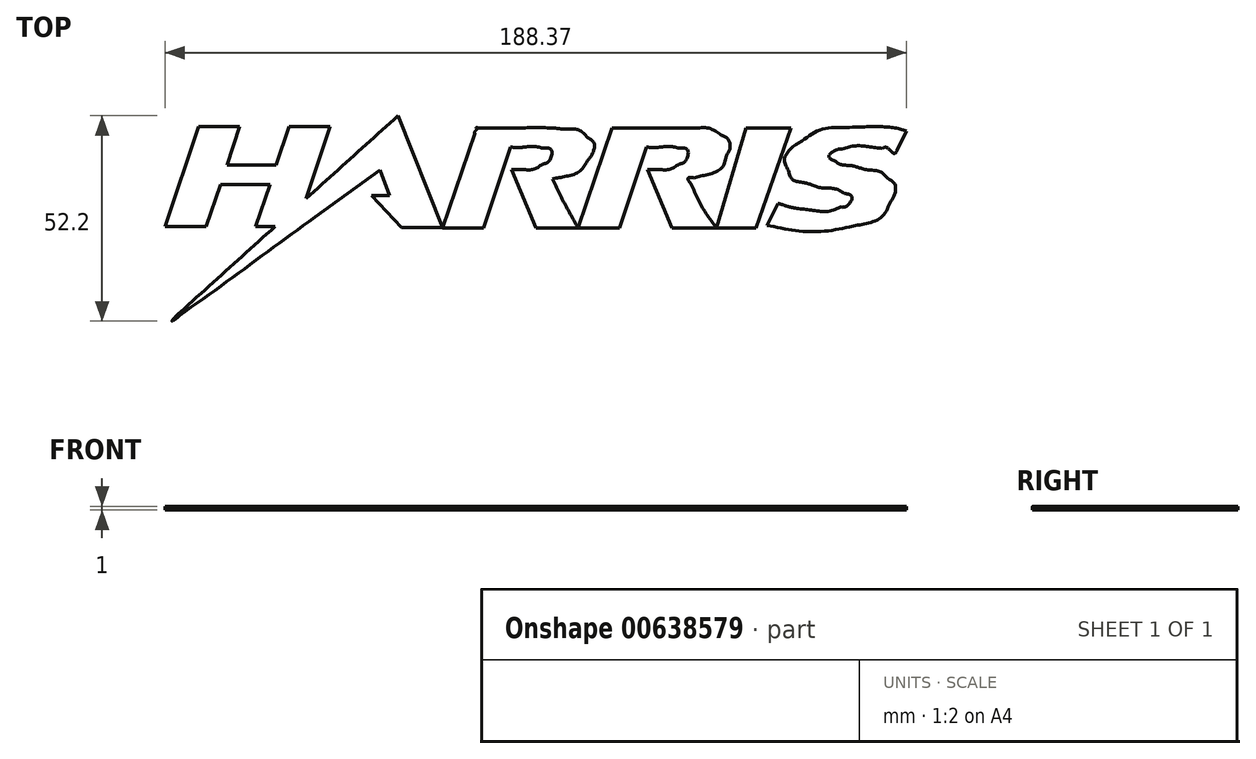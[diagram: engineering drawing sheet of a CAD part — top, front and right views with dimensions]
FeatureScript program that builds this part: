
annotation { "Feature Type Name" : "Feature", "Feature Type Description" : "" }
export const myFeature = defineFeature(function(context is Context, id is Id, definition is map)
    precondition{}
    {
        {
            var Q0;
            Q0=qCreatedBy(makeId("Top.planeOp"),FACE);
            var sketch = newSketch(context, id + "F0", { "sketchPlane" : qUnion([Q0])});
            skFitSpline(sketch, "E0", {"points": [v(65, 22.87) * mm, v(59.37, 22.73) * mm, v(53.44, 22.23) * mm, v(48.5, 19.25) * mm]});
            skFitSpline(sketch, "E1", {"points": [v(48.5, 19.25) * mm, v(46.1, 17.74) * mm, v(44, 14.7) * mm, v(45.01, 11.78) * mm]});
            skFitSpline(sketch, "E2", {"points": [v(45.01, 11.78) * mm, v(46.07, 9.46) * mm, v(48.77, 8.71) * mm, v(51.04, 8.09) * mm]});
            skFitSpline(sketch, "E3", {"points": [v(51.04, 8.09) * mm, v(53.74, 7.3) * mm, v(56.65, 7.17) * mm, v(59.22, 5.95) * mm]});
            skFitSpline(sketch, "E4", {"points": [v(59.22, 5.95) * mm, v(61.14, 5.03) * mm, v(59.79, 2.74) * mm, v(58.18, 2.44) * mm]});
            skFitSpline(sketch, "E5", {"points": [v(58.18, 2.44) * mm, v(54.76, 1.33) * mm, v(51.07, 1.66) * mm, v(47.55, 2.08) * mm]});
            skFitSpline(sketch, "E6", {"points": [v(47.55, 2.08) * mm, v(45.8, 2.37) * mm, v(44.07, 2.88) * mm, v(42.37, 3.4) * mm]});
            skFitSpline(sketch, "E7", {"points": [v(42.37, 3.4) * mm, v(41.43, 1.55) * mm, v(40.5, -0.3) * mm, v(39.57, -2.15) * mm]});
            skFitSpline(sketch, "E8", {"points": [v(39.57, -2.15) * mm, v(46.47, -3.44) * mm, v(53.6, -3.71) * mm, v(60.53, -2.54) * mm]});
            skFitSpline(sketch, "E9", {"points": [v(60.53, -2.54) * mm, v(64.47, -1.76) * mm, v(68.66, -0.09) * mm, v(70.77, 3.54) * mm]});
            skFitSpline(sketch, "E10", {"points": [v(70.77, 3.54) * mm, v(71.9, 5.4) * mm, v(72.08, 8.13) * mm, v(70.32, 9.67) * mm]});
            skFitSpline(sketch, "E11", {"points": [v(70.32, 9.67) * mm, v(68.23, 11.51) * mm, v(65.34, 11.9) * mm, v(62.73, 12.54) * mm]});
            skFitSpline(sketch, "E12", {"points": [v(62.73, 12.54) * mm, v(60.76, 13.03) * mm, v(58.65, 13.2) * mm, v(56.82, 14.13) * mm]});
            skFitSpline(sketch, "E13", {"points": [v(56.82, 14.13) * mm, v(55.27, 15.4) * mm, v(57.28, 17.05) * mm, v(58.65, 17.24) * mm]});
            skFitSpline(sketch, "E14", {"points": [v(58.65, 17.24) * mm, v(62, 18.03) * mm, v(65.5, 17.8) * mm, v(68.88, 17.36) * mm]});
            skFitSpline(sketch, "E15", {"points": [v(68.88, 17.36) * mm, v(70.04, 17.6) * mm, v(71.86, 16.04) * mm, v(72.58, 16.89) * mm]});
            skFitSpline(sketch, "E16", {"points": [v(72.58, 16.89) * mm, v(73.39, 18.54) * mm, v(74.2, 20.18) * mm, v(75, 21.83) * mm]});
            skFitSpline(sketch, "E17", {"points": [v(75, 21.83) * mm, v(71.75, 22.62) * mm, v(68.34, 22.89) * mm, v(65, 22.87) * mm]});
            skLineSegment(sketch, "E18", {"start": v(-104.86, 22.9) * mm, "end": v(-113.37, -2.5) * mm});
            skLineSegment(sketch, "E19", {"start": v(-113.37, -2.5) * mm, "end": v(-102.93, -2.5) * mm});
            skLineSegment(sketch, "E20", {"start": v(-102.93, -2.5) * mm, "end": v(-99.31, 8.26) * mm});
            skLineSegment(sketch, "E21", {"start": v(-99.31, 8.26) * mm, "end": v(-86.73, 8.26) * mm});
            skLineSegment(sketch, "E22", {"start": v(-86.73, 8.26) * mm, "end": v(-90.35, -2.5) * mm});
            skLineSegment(sketch, "E23", {"start": v(-90.35, -2.5) * mm, "end": v(-85.18, -2.5) * mm});
            skLineSegment(sketch, "E24", {"start": v(-85.18, -2.5) * mm, "end": v(-77.6, 4.33) * mm});
            skLineSegment(sketch, "E25", {"start": v(-77.6, 4.33) * mm, "end": v(-71.4, 22.9) * mm});
            skLineSegment(sketch, "E26", {"start": v(-71.4, 22.9) * mm, "end": v(-81.84, 22.9) * mm});
            skLineSegment(sketch, "E27", {"start": v(-81.84, 22.9) * mm, "end": v(-85.11, 13.15) * mm});
            skLineSegment(sketch, "E28", {"start": v(-85.11, 13.15) * mm, "end": v(-97.66, 13.15) * mm});
            skLineSegment(sketch, "E29", {"start": v(-97.66, 13.15) * mm, "end": v(-94.38, 22.9) * mm});
            skLineSegment(sketch, "E30", {"start": v(-94.38, 22.9) * mm, "end": v(-104.86, 22.9) * mm});
            skLineSegment(sketch, "E31", {"start": v(-104.86, 22.9) * mm, "end": v(-104.86, 22.9) * mm});
            skFitSpline(sketch, "E32", {"points": [v(-11.94, 3.53) * mm, v(-13.01, 5.53) * mm, v(-13.98, 7.58) * mm, v(-14.94, 9.63) * mm]});
            skFitSpline(sketch, "E33", {"points": [v(-14.94, 9.63) * mm, v(-11.66, 10.25) * mm, v(-8.13, 11.47) * mm, v(-6.07, 14.26) * mm]});
            skFitSpline(sketch, "E34", {"points": [v(-6.07, 14.26) * mm, v(-4.83, 15.93) * mm, v(-4.36, 18.58) * mm, v(-6.03, 20.14) * mm]});
            skFitSpline(sketch, "E35", {"points": [v(-6.03, 20.14) * mm, v(-8.27, 22.06) * mm, v(-11.39, 22.3) * mm, v(-14.2, 22.52) * mm]});
            skFitSpline(sketch, "E36", {"points": [v(-14.2, 22.52) * mm, v(-19.17, 22.67) * mm, v(-24.14, 22.56) * mm, v(-29.1, 22.6) * mm]});
            skFitSpline(sketch, "E37", {"points": [v(-29.1, 22.6) * mm, v(-30.88, 22.6) * mm, v(-32.67, 22.6) * mm, v(-34.45, 22.6) * mm]});
            skFitSpline(sketch, "E38", {"points": [v(-34.45, 22.6) * mm, v(-33.92, 22.6) * mm, v(-34.66, 21.63) * mm, v(-34.67, 21.22) * mm]});
            skFitSpline(sketch, "E39", {"points": [v(-34.67, 21.22) * mm, v(-37.38, 13.22) * mm, v(-40.1, 5.21) * mm, v(-42.81, -2.8) * mm]});
            skFitSpline(sketch, "E40", {"points": [v(-42.81, -2.8) * mm, v(-39.38, -2.8) * mm, v(-35.95, -2.8) * mm, v(-32.52, -2.8) * mm]});
            skFitSpline(sketch, "E41", {"points": [v(-32.52, -2.8) * mm, v(-30.22, 4.03) * mm, v(-27.92, 10.86) * mm, v(-25.63, 17.7) * mm]});
            skFitSpline(sketch, "E42", {"points": [v(-25.63, 17.7) * mm, v(-22.86, 17.63) * mm, v(-20.06, 17.89) * mm, v(-17.32, 17.42) * mm]});
            skFitSpline(sketch, "E43", {"points": [v(-17.32, 17.42) * mm, v(-15.18, 17) * mm, v(-15.88, 14.1) * mm, v(-17.45, 13.4) * mm]});
            skFitSpline(sketch, "E44", {"points": [v(-17.45, 13.4) * mm, v(-19.84, 12.06) * mm, v(-22.7, 12.01) * mm, v(-25.38, 12.01) * mm]});
            skFitSpline(sketch, "E45", {"points": [v(-25.38, 12.01) * mm, v(-23.32, 7.07) * mm, v(-21.25, 2.13) * mm, v(-19.18, -2.8) * mm]});
            skFitSpline(sketch, "E46", {"points": [v(-19.18, -2.8) * mm, v(-15.6, -2.81) * mm, v(-12.02, -2.82) * mm, v(-8.44, -2.83) * mm]});
            skFitSpline(sketch, "E47", {"points": [v(-8.44, -2.83) * mm, v(-9.62, -0.71) * mm, v(-10.8, 1.4) * mm, v(-11.94, 3.53) * mm]});
            skLineSegment(sketch, "E48", {"start": v(-11.94, 3.53) * mm, "end": v(-11.94, 3.53) * mm});
            skFitSpline(sketch, "E49", {"points": [v(2.09, -2.8) * mm, v(4.39, 4.03) * mm, v(6.68, 10.86) * mm, v(8.98, 17.7) * mm]});
            skFitSpline(sketch, "E50", {"points": [v(8.98, 17.7) * mm, v(11.75, 17.63) * mm, v(14.55, 17.89) * mm, v(17.29, 17.42) * mm]});
            skFitSpline(sketch, "E51", {"points": [v(17.29, 17.42) * mm, v(19.42, 17) * mm, v(18.78, 14.1) * mm, v(17.2, 13.4) * mm]});
            skFitSpline(sketch, "E52", {"points": [v(17.2, 13.4) * mm, v(14.79, 12.06) * mm, v(11.92, 12.01) * mm, v(9.22, 12.01) * mm]});
            skFitSpline(sketch, "E53", {"points": [v(9.22, 12.01) * mm, v(11.3, 7.07) * mm, v(13.36, 2.13) * mm, v(15.43, -2.8) * mm]});
            skFitSpline(sketch, "E54", {"points": [v(15.43, -2.8) * mm, v(19.2, -2.8) * mm, v(22.96, -2.8) * mm, v(26.73, -2.8) * mm]});
            skFitSpline(sketch, "E55", {"points": [v(26.73, -2.8) * mm, v(24.2, 0.67) * mm, v(22.04, 4.4) * mm, v(20.28, 8.32) * mm]});
            skFitSpline(sketch, "E56", {"points": [v(20.28, 8.32) * mm, v(19.56, 9.33) * mm, v(19.6, 9.92) * mm, v(20.96, 9.89) * mm]});
            skFitSpline(sketch, "E57", {"points": [v(20.96, 9.89) * mm, v(24.23, 10.7) * mm, v(27.9, 12.24) * mm, v(29.28, 15.58) * mm]});
            skFitSpline(sketch, "E58", {"points": [v(29.28, 15.58) * mm, v(30.12, 17.32) * mm, v(29.7, 19.66) * mm, v(27.95, 20.68) * mm]});
            skFitSpline(sketch, "E59", {"points": [v(27.95, 20.68) * mm, v(24.92, 22.46) * mm, v(21.28, 22.52) * mm, v(17.87, 22.6) * mm]});
            skFitSpline(sketch, "E60", {"points": [v(17.87, 22.6) * mm, v(11.97, 22.6) * mm, v(6.06, 22.6) * mm, v(0.16, 22.6) * mm]});
            skFitSpline(sketch, "E61", {"points": [v(0.16, 22.6) * mm, v(-2.7, 14.12) * mm, v(-5.57, 5.65) * mm, v(-8.44, -2.83) * mm]});
            skFitSpline(sketch, "E62", {"points": [v(-8.44, -2.83) * mm, v(-4.93, -2.82) * mm, v(-1.42, -2.81) * mm, v(2.09, -2.8) * mm]});
            skLineSegment(sketch, "E63", {"start": v(2.09, -2.8) * mm, "end": v(2.09, -2.8) * mm});
            skLineSegment(sketch, "E64", {"start": v(36.8, -2.8) * mm, "end": v(45.66, 22.6) * mm});
            skLineSegment(sketch, "E65", {"start": v(45.66, 22.6) * mm, "end": v(34.26, 22.6) * mm});
            skLineSegment(sketch, "E66", {"start": v(34.26, 22.6) * mm, "end": v(26.73, -2.8) * mm});
            skLineSegment(sketch, "E67", {"start": v(26.73, -2.8) * mm, "end": v(36.8, -2.8) * mm});
            skFitSpline(sketch, "E68", {"points": [v(-54.16, 25.67) * mm, v(-72.6, 9.04) * mm, v(-91.05, -7.56) * mm, v(-109.48, -24.2) * mm]});
            skFitSpline(sketch, "E69", {"points": [v(-109.48, -24.2) * mm, v(-110.47, -25.16) * mm, v(-111.61, -26.52) * mm, v(-109.72, -25.12) * mm]});
            skFitSpline(sketch, "E70", {"points": [v(-109.72, -25.12) * mm, v(-98.17, -16.86) * mm, v(-86.75, -8.43) * mm, v(-75.25, -0.1) * mm]});
            skFitSpline(sketch, "E71", {"points": [v(-75.25, -0.1) * mm, v(-69.75, 3.9) * mm, v(-64.24, 7.9) * mm, v(-58.74, 11.9) * mm]});
            skFitSpline(sketch, "E72", {"points": [v(-58.74, 11.9) * mm, v(-57.95, 9.74) * mm, v(-57.16, 7.58) * mm, v(-56.37, 5.4) * mm]});
            skFitSpline(sketch, "E73", {"points": [v(-56.37, 5.4) * mm, v(-57.89, 5.4) * mm, v(-59.4, 5.4) * mm, v(-60.92, 5.4) * mm]});
            skFitSpline(sketch, "E74", {"points": [v(-60.92, 5.4) * mm, v(-58.37, 2.68) * mm, v(-55.82, -0.04) * mm, v(-53.27, -2.77) * mm]});
            skFitSpline(sketch, "E75", {"points": [v(-53.27, -2.77) * mm, v(-49.79, -2.77) * mm, v(-46.3, -2.77) * mm, v(-42.81, -2.77) * mm]});
            skFitSpline(sketch, "E76", {"points": [v(-42.81, -2.77) * mm, v(-46.6, 6.71) * mm, v(-50.38, 16.2) * mm, v(-54.16, 25.67) * mm]});
            skSolve(sketch);
        }
        {
            var Q0;
            Q0 = qSketchRegion(id + "F0", true);
            extrude(context, id + "F1", {"entities" : qUnion([Q0]), "depth" : 1 * mm, "offsetDistance" : 25.4 * mm});
        }
    });
